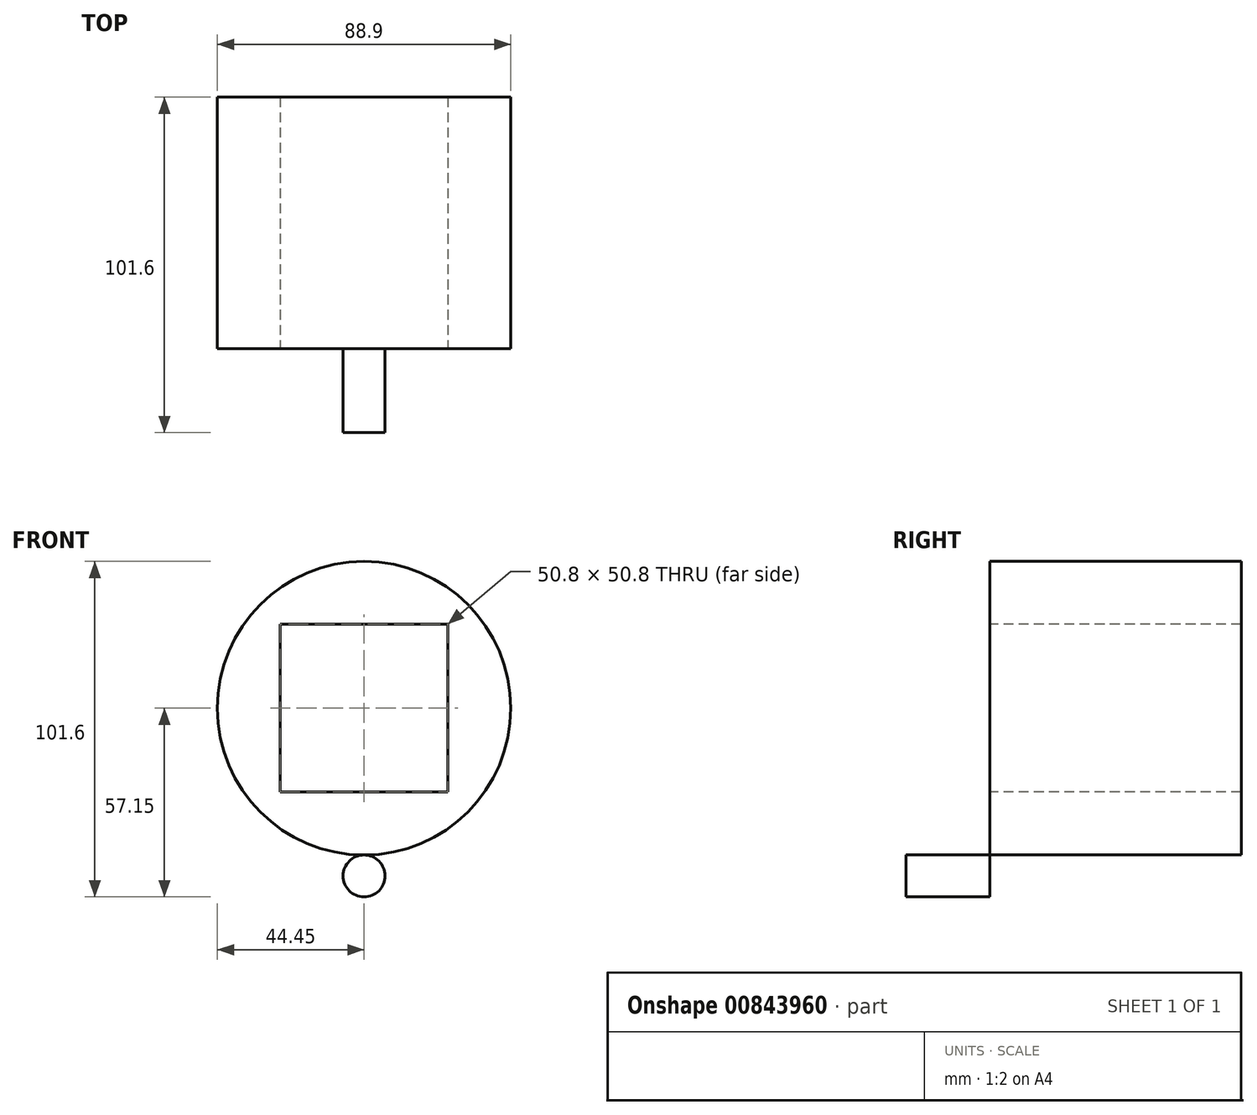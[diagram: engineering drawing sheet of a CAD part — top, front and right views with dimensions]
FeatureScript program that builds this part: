
annotation { "Feature Type Name" : "Feature", "Feature Type Description" : "" }
export const myFeature = defineFeature(function(context is Context, id is Id, definition is map)
    precondition{}
    {
        {
            var Q0;
            Q0=qCreatedBy(makeId("Front.planeOp"),FACE);
            var sketch = newSketch(context, id + "F0", { "sketchPlane" : qUnion([Q0])});
            skCircle(sketch, "E0", {"center": v(0, 0) * mm, "radius": 63.5 * mm});
            skSolve(sketch);
        }
        {
            var Q0;
            Q0 = qSketchRegion(id + "F0", true);
            extrude(context, id + "F1", {"entities" : qUnion([Q0]), "depth" : 25.4 * mm, "offsetDistance" : 25.4 * mm});
        }
        {
            var Q0;
            Q0=makeQuery(id+"F1.opExtrude","CAP_FACE",FACE,{"disambiguationData":[OSD([sQuery(id+"F0.wireOp",EDGE,"E0")])],"isStart":false});
            var sketch = newSketch(context, id + "F2", { "sketchPlane" : qUnion([Q0])});
            skCircle(sketch, "E1", {"center": v(0, 0) * mm, "radius": 50.8 * mm});
            skCircle(sketch, "E2", {"center": v(0, 50.8) * mm, "radius": 6.35 * mm});
            skSolve(sketch);
        }
        {
            var Q0;
            {var subQ0=sQuery(id+"F2.wireOp",EDGE,"E2");var subQ1=sQuery(id+"F2.wireOp",EDGE,"E1");var subQ2=makeQuery(id+"F2.imprint","INTERSECT",VERTEX,{"disambiguationData":[OD(0.0)],"derivedFrom":[subQ1,subQ0]});Q0=makeQuery(id+"F2.imprint","IMPRINT",FACE,{"disambiguationData":[TD([[makeQuery(id+"F2.imprint","IMPRINT",EDGE,{"disambiguationData":[TD([[subQ2,1.0]])],"derivedFrom":subQ1}),-1.0]])]});}
            var Q1;
            {var subQ0=sQuery(id+"F2.wireOp",EDGE,"E2");var subQ1=sQuery(id+"F2.wireOp",EDGE,"E1");var subQ2=makeQuery(id+"F2.imprint","INTERSECT",VERTEX,{"disambiguationData":[OD(0.0)],"derivedFrom":[subQ1,subQ0]});Q1=makeQuery(id+"F2.imprint","IMPRINT",FACE,{"disambiguationData":[TD([[makeQuery(id+"F2.imprint","IMPRINT",EDGE,{"disambiguationData":[TD([[subQ2,1.0]])],"derivedFrom":subQ1}),1.0]])]});}
            extrude(context, id + "F3", {"entities" : qUnion([Q0, Q1]), "operationType" : NewBodyOperationType.REMOVE, "oppositeDirection" : true, "depth" : 25.4 * mm, "offsetDistance" : 25.4 * mm});
        }
        {
            var Q0;
            Q0=makeQuery(id+"F1.opExtrude","CAP_FACE",FACE,{"disambiguationData":[OSD([sQuery(id+"F0.wireOp",EDGE,"E0")])],"isStart":false});
            var sketch = newSketch(context, id + "F4", { "sketchPlane" : qUnion([Q0])});
            skCircle(sketch, "E3", {"center": v(0, 0) * mm, "radius": 50.8 * mm});
            skCircle(sketch, "E4", {"center": v(50.8, 0) * mm, "radius": 6.35 * mm});
            skCircle(sketch, "E5", {"center": v(0, -50.8) * mm, "radius": 6.35 * mm});
            skCircle(sketch, "E6", {"center": v(-50.8, 0) * mm, "radius": 6.35 * mm});
            skSolve(sketch);
        }
        {
            var Q0;
            {var subQ0=sQuery(id+"F4.wireOp",EDGE,"E6");var subQ1=sQuery(id+"F4.wireOp",EDGE,"E3");var subQ2=makeQuery(id+"F4.imprint","INTERSECT",VERTEX,{"disambiguationData":[OD(0.0)],"derivedFrom":[subQ1,subQ0]});Q0=makeQuery(id+"F4.imprint","IMPRINT",FACE,{"disambiguationData":[TD([[makeQuery(id+"F4.imprint","IMPRINT",EDGE,{"disambiguationData":[TD([[subQ2,-1.0]])],"derivedFrom":subQ1}),1.0]])]});}
            var Q1;
            {var subQ0=sQuery(id+"F4.wireOp",EDGE,"E6");var subQ1=sQuery(id+"F4.wireOp",EDGE,"E3");var subQ2=makeQuery(id+"F4.imprint","INTERSECT",VERTEX,{"disambiguationData":[OD(0.0)],"derivedFrom":[subQ1,subQ0]});Q1=makeQuery(id+"F4.imprint","IMPRINT",FACE,{"disambiguationData":[TD([[makeQuery(id+"F4.imprint","IMPRINT",EDGE,{"disambiguationData":[TD([[subQ2,-1.0]])],"derivedFrom":subQ1}),-1.0]])]});}
            extrude(context, id + "F5", {"entities" : qUnion([Q0, Q1]), "operationType" : NewBodyOperationType.REMOVE, "oppositeDirection" : true, "depth" : 25.4 * mm, "offsetDistance" : 25.4 * mm});
        }
        {
            var Q0;
            Q0=makeQuery(id+"F1.opExtrude","CAP_FACE",FACE,{"disambiguationData":[OSD([sQuery(id+"F0.wireOp",EDGE,"E0")])],"isStart":false});
            var sketch = newSketch(context, id + "F6", { "sketchPlane" : qUnion([Q0])});
            skCircle(sketch, "E7", {"center": v(0, 0) * mm, "radius": 50.8 * mm});
            skCircle(sketch, "E8", {"center": v(50.8, 0) * mm, "radius": 6.35 * mm});
            skSolve(sketch);
        }
        {
            var Q0;
            {var subQ0=sQuery(id+"F6.wireOp",EDGE,"E8");var subQ1=sQuery(id+"F6.wireOp",EDGE,"E7");var subQ2=makeQuery(id+"F6.imprint","INTERSECT",VERTEX,{"disambiguationData":[OD(0.0)],"derivedFrom":[subQ1,subQ0]});Q0=makeQuery(id+"F6.imprint","IMPRINT",FACE,{"disambiguationData":[TD([[makeQuery(id+"F6.imprint","IMPRINT",EDGE,{"disambiguationData":[TD([[subQ2,1.0]])],"derivedFrom":subQ1}),1.0]])]});}
            var sketch = newSketch(context, id + "F7", { "sketchPlane" : qUnion([Q0])});
            skSolve(sketch);
        }
        {
            var Q0;
            {var subQ0=sQuery(id+"F6.wireOp",EDGE,"E8");var subQ1=sQuery(id+"F6.wireOp",EDGE,"E7");var subQ2=makeQuery(id+"F6.imprint","INTERSECT",VERTEX,{"disambiguationData":[OD(0.0)],"derivedFrom":[subQ1,subQ0]});Q0=makeQuery(id+"F6.imprint","IMPRINT",FACE,{"disambiguationData":[TD([[makeQuery(id+"F6.imprint","IMPRINT",EDGE,{"disambiguationData":[TD([[subQ2,1.0]])],"derivedFrom":subQ1}),-1.0]])]});}
            var Q1;
            {var subQ0=sQuery(id+"F6.wireOp",EDGE,"E8");var subQ1=sQuery(id+"F6.wireOp",EDGE,"E7");var subQ2=makeQuery(id+"F6.imprint","INTERSECT",VERTEX,{"disambiguationData":[OD(0.0)],"derivedFrom":[subQ1,subQ0]});Q1=makeQuery(id+"F7.imprint","IMPRINT",FACE,{"disambiguationData":[TD([[makeQuery(id+"F7.imprint","IMPRINT",EDGE,{"derivedFrom":makeQuery(id+"F6.imprint","IMPRINT",EDGE,{"disambiguationData":[TD([[subQ2,1.0]])],"derivedFrom":subQ1})}),1.0]])]});}
            extrude(context, id + "F8", {"entities" : qUnion([Q0, Q1]), "operationType" : NewBodyOperationType.REMOVE, "oppositeDirection" : true, "depth" : 25.4 * mm, "offsetDistance" : 25.4 * mm});
        }
        {
            var Q0;
            Q0=makeQuery(id+"F1.opExtrude","CAP_FACE",FACE,{"disambiguationData":[OSD([sQuery(id+"F0.wireOp",EDGE,"E0")])],"isStart":false});
            var sketch = newSketch(context, id + "F9", { "sketchPlane" : qUnion([Q0])});
            skCircle(sketch, "E9", {"center": v(0, 0) * mm, "radius": 50.8 * mm});
            skCircle(sketch, "E10", {"center": v(0, -50.8) * mm, "radius": 6.35 * mm});
            skSolve(sketch);
        }
        {
            var Q0;
            {var subQ0=sQuery(id+"F9.wireOp",EDGE,"E9");var subQ1=makeQuery(id+"F3.boolean.opBoolean","COPY",EDGE,{"derivedFrom":makeQuery(id+"F3.opExtrude","CAP_EDGE",EDGE,{"disambiguationData":[OSD([sQuery(id+"F2.wireOp",EDGE,"E2")])],"isStart":true})});var subQ2=makeQuery(id+"F9.imprint","INTERSECT",VERTEX,{"disambiguationData":[OD(0.0)],"derivedFrom":[subQ1,subQ0]});Q0=makeQuery(id+"F9.imprint","IMPRINT",FACE,{"disambiguationData":[TD([[makeQuery(id+"F9.imprint","IMPRINT",EDGE,{"disambiguationData":[TD([[subQ2,-1.0]])],"derivedFrom":subQ0}),1.0]])]});}
            var Q1;
            {var subQ0=sQuery(id+"F9.wireOp",EDGE,"E9");var subQ1=makeQuery(id+"F5.boolean.opBoolean","COPY",EDGE,{"derivedFrom":makeQuery(id+"F5.opExtrude","CAP_EDGE",EDGE,{"disambiguationData":[OSD([sQuery(id+"F4.wireOp",EDGE,"E6")])],"isStart":true})});var subQ2=makeQuery(id+"F9.imprint","INTERSECT",VERTEX,{"disambiguationData":[OD(0.0)],"derivedFrom":[subQ1,subQ0]});Q1=makeQuery(id+"F9.imprint","IMPRINT",FACE,{"disambiguationData":[TD([[makeQuery(id+"F9.imprint","IMPRINT",EDGE,{"disambiguationData":[TD([[subQ2,-1.0]])],"derivedFrom":subQ0}),1.0]])]});}
            var Q2;
            {var subQ0=sQuery(id+"F9.wireOp",EDGE,"E9");var subQ1=sQuery(id+"F6.wireOp",EDGE,"E8");var subQ2=sQuery(id+"F6.wireOp",EDGE,"E7");var subQ3=makeQuery(id+"F6.imprint","INTERSECT",VERTEX,{"disambiguationData":[OD(0.0)],"derivedFrom":[subQ2,subQ1]});var subQ5=makeQuery(id+"F8.boolean.opBoolean","TWEAK_EDGE",EDGE,{"derivedFrom":[makeQuery(id+"F8.opExtrude","CAP_EDGE",EDGE,{"disambiguationData":[OSD([subQ1]),TDD([makeQuery(id+"F6.imprint","IMPRINT",EDGE,{"disambiguationData":[TD([[subQ3,1.0]])],"derivedFrom":subQ1})])],"isStart":true}),makeQuery(id+"F8.opExtrude","CAP_EDGE",EDGE,{"disambiguationData":[OSD([subQ1]),TDD([makeQuery(id+"F7.imprint","IMPRINT",EDGE,{"derivedFrom":makeQuery(id+"F6.imprint","IMPRINT",EDGE,{"disambiguationData":[TD([[subQ3,-1.0]])],"derivedFrom":subQ1})})])],"isStart":true})]});var subQ6=makeQuery(id+"F9.imprint","INTERSECT",VERTEX,{"disambiguationData":[OD(0.0)],"derivedFrom":[subQ5,subQ0]});Q2=makeQuery(id+"F9.imprint","IMPRINT",FACE,{"disambiguationData":[TD([[makeQuery(id+"F9.imprint","IMPRINT",EDGE,{"disambiguationData":[TD([[subQ6,1.0]])],"derivedFrom":subQ0}),1.0]])]});}
            var Q3;
            {var subQ0=sQuery(id+"F9.wireOp",EDGE,"E10");var subQ1=sQuery(id+"F9.wireOp",EDGE,"E9");var subQ2=makeQuery(id+"F9.imprint","INTERSECT",VERTEX,{"disambiguationData":[OD(0.0)],"derivedFrom":[subQ1,subQ0]});Q3=makeQuery(id+"F9.imprint","IMPRINT",FACE,{"disambiguationData":[TD([[makeQuery(id+"F9.imprint","IMPRINT",EDGE,{"disambiguationData":[TD([[subQ2,-1.0]])],"derivedFrom":subQ1}),-1.0]])]});}
            var Q4;
            {var subQ0=sQuery(id+"F9.wireOp",EDGE,"E10");var subQ1=sQuery(id+"F9.wireOp",EDGE,"E9");var subQ2=makeQuery(id+"F9.imprint","INTERSECT",VERTEX,{"disambiguationData":[OD(0.0)],"derivedFrom":[subQ1,subQ0]});Q4=makeQuery(id+"F9.imprint","IMPRINT",FACE,{"disambiguationData":[TD([[makeQuery(id+"F9.imprint","IMPRINT",EDGE,{"disambiguationData":[TD([[subQ2,-1.0]])],"derivedFrom":subQ1}),1.0]])]});}
            extrude(context, id + "F10", {"entities" : qUnion([Q0, Q1, Q2, Q3, Q4]), "operationType" : NewBodyOperationType.REMOVE, "oppositeDirection" : true, "depth" : 25.4 * mm, "offsetDistance" : 25.4 * mm});
        }
        {
            var Q0;
            Q0=makeQuery(id+"F1.opExtrude","CAP_FACE",FACE,{"disambiguationData":[OSD([sQuery(id+"F0.wireOp",EDGE,"E0")])],"isStart":true});
            var sketch = newSketch(context, id + "F11", { "sketchPlane" : qUnion([Q0])});
            skCircle(sketch, "E11", {"center": v(0, 0) * mm, "radius": 44.45 * mm});
            skSolve(sketch);
        }
        {
            var Q0;
            Q0 = qSketchRegion(id + "F11", true);
            extrude(context, id + "F12", {"entities" : qUnion([Q0]), "operationType" : NewBodyOperationType.ADD, "depth" : 76.2 * mm, "offsetDistance" : 25.4 * mm});
        }
        {
            var Q0;
            Q0=makeQuery(id+"F1.opExtrude","CAP_FACE",FACE,{"disambiguationData":[OSD([sQuery(id+"F0.wireOp",EDGE,"E0")])],"isStart":false});
            var sketch = newSketch(context, id + "F13", { "sketchPlane" : qUnion([Q0])});
            skLineSegment(sketch, "E12.bottom", {"start": v(-25.4, 25.4) * mm, "end": v(25.4, 25.4) * mm});
            skLineSegment(sketch, "E12.top", {"start": v(-25.4, -25.4) * mm, "end": v(25.4, -25.4) * mm});
            skLineSegment(sketch, "E12.left", {"start": v(-25.4, 25.4) * mm, "end": v(-25.4, -25.4) * mm});
            skLineSegment(sketch, "E12.right", {"start": v(25.4, 25.4) * mm, "end": v(25.4, -25.4) * mm});
            skSolve(sketch);
        }
        {
            var Q0;
            Q0=makeQuery(id+"F13.imprint","IMPRINT",FACE,{"disambiguationData":[TD([[makeQuery(id+"F13.imprint","IMPRINT",EDGE,{"derivedFrom":sQuery(id+"F13.wireOp",EDGE,"E12.bottom")}),-1.0]])]});
            extrude(context, id + "F14", {"entities" : qUnion([Q0]), "operationType" : NewBodyOperationType.REMOVE, "oppositeDirection" : true, "depth" : 254 * mm, "offsetDistance" : 25.4 * mm});
        }
    });
